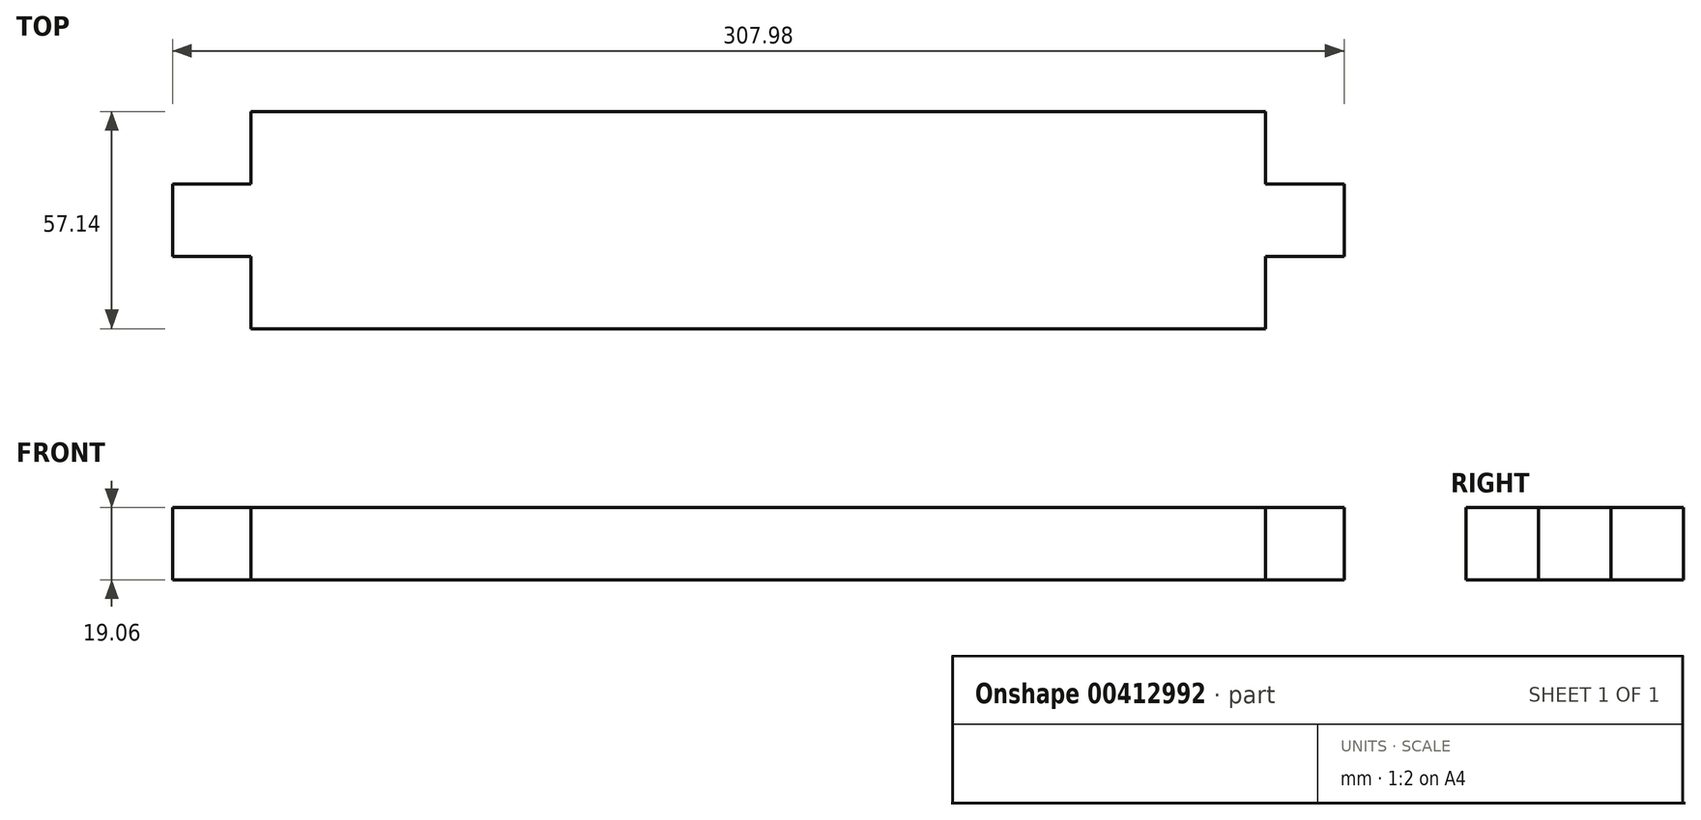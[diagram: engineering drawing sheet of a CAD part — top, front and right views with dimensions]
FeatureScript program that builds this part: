
annotation { "Feature Type Name" : "Feature", "Feature Type Description" : "" }
export const myFeature = defineFeature(function(context is Context, id is Id, definition is map)
    precondition{}
    {
        {
            var Q0;
            Q0=qCreatedBy(makeId("Top.planeOp"),FACE);
            var sketch = newSketch(context, id + "F0", { "sketchPlane" : qUnion([Q0])});
            skLineSegment(sketch, "E0.bottom", {"start": v(-153.99, 28.57) * mm, "end": v(153.99, 28.58) * mm});
            skLineSegment(sketch, "E0.top", {"start": v(-153.99, -28.58) * mm, "end": v(153.99, -28.57) * mm});
            skLineSegment(sketch, "E0.left", {"start": v(-153.99, 28.58) * mm, "end": v(-153.99, -28.58) * mm});
            skLineSegment(sketch, "E0.right", {"start": v(153.99, 28.58) * mm, "end": v(153.99, -28.58) * mm});
            skSolve(sketch);
        }
        {
            var Q0;
            Q0=makeQuery(id+"F0.imprint","IMPRINT",FACE,{"disambiguationData":[TD([[makeQuery(id+"F0.imprint","IMPRINT",EDGE,{"derivedFrom":sQuery(id+"F0.wireOp",EDGE,"E0.bottom")}),-1.0]])]});
            extrude(context, id + "F1", {"entities" : qUnion([Q0]), "endBound" : BoundingType.SYMMETRIC, "depth" : 19.05 * mm});
        }
        {
            var Q0;
            Q0=makeQuery(id+"F1.opExtrude","CAP_FACE",FACE,{"disambiguationData":[OSD([sQuery(id+"F0.wireOp",EDGE,"E0.bottom"),sQuery(id+"F0.wireOp",EDGE,"E0.top"),sQuery(id+"F0.wireOp",EDGE,"E0.left"),sQuery(id+"F0.wireOp",EDGE,"E0.right")])],"isStart":false});
            var sketch = newSketch(context, id + "F2", { "sketchPlane" : qUnion([Q0])});
            skLineSegment(sketch, "E1.bottom", {"start": v(-153.99, 28.57) * mm, "end": v(-133.35, 28.57) * mm});
            skLineSegment(sketch, "E1.top", {"start": v(-153.99, 9.52) * mm, "end": v(-133.35, 9.52) * mm});
            skLineSegment(sketch, "E1.left", {"start": v(-153.99, 28.57) * mm, "end": v(-153.99, 9.52) * mm});
            skLineSegment(sketch, "E1.right", {"start": v(-133.35, 28.57) * mm, "end": v(-133.35, 9.52) * mm});
            skLineSegment(sketch, "E2.bottom", {"start": v(-153.99, -28.58) * mm, "end": v(-133.35, -28.58) * mm});
            skLineSegment(sketch, "E2.top", {"start": v(-153.99, -9.53) * mm, "end": v(-133.35, -9.53) * mm});
            skLineSegment(sketch, "E2.left", {"start": v(-153.99, -28.58) * mm, "end": v(-153.99, -9.53) * mm});
            skLineSegment(sketch, "E2.right", {"start": v(-133.35, -28.58) * mm, "end": v(-133.35, -9.53) * mm});
            skLineSegment(sketch, "E3.MirrorCS", {"start": v(153.99, 28.57) * mm, "end": v(153.99, 9.52) * mm});
            skLineSegment(sketch, "E4.MirrorCS", {"start": v(153.99, 28.57) * mm, "end": v(133.35, 28.57) * mm});
            skLineSegment(sketch, "E5.MirrorCS", {"start": v(133.35, 28.57) * mm, "end": v(133.35, 9.52) * mm});
            skLineSegment(sketch, "E6.MirrorCS", {"start": v(153.99, 9.52) * mm, "end": v(133.35, 9.52) * mm});
            skLineSegment(sketch, "E7.MirrorCS", {"start": v(153.99, -28.58) * mm, "end": v(153.99, -9.53) * mm});
            skLineSegment(sketch, "E8.MirrorCS", {"start": v(153.99, -9.53) * mm, "end": v(133.35, -9.53) * mm});
            skLineSegment(sketch, "E9.MirrorCS", {"start": v(133.35, -28.58) * mm, "end": v(133.35, -9.53) * mm});
            skLineSegment(sketch, "E10.MirrorCS", {"start": v(153.99, -28.58) * mm, "end": v(133.35, -28.58) * mm});
            skSolve(sketch);
        }
        {
            var Q0;
            Q0 = qSketchRegion(id + "F2", true);
            extrude(context, id + "F3", {"entities" : qUnion([Q0]), "operationType" : NewBodyOperationType.REMOVE, "endBound" : BoundingType.THROUGH_ALL, "oppositeDirection" : true, "depth" : 25.4 * mm});
        }
    });
